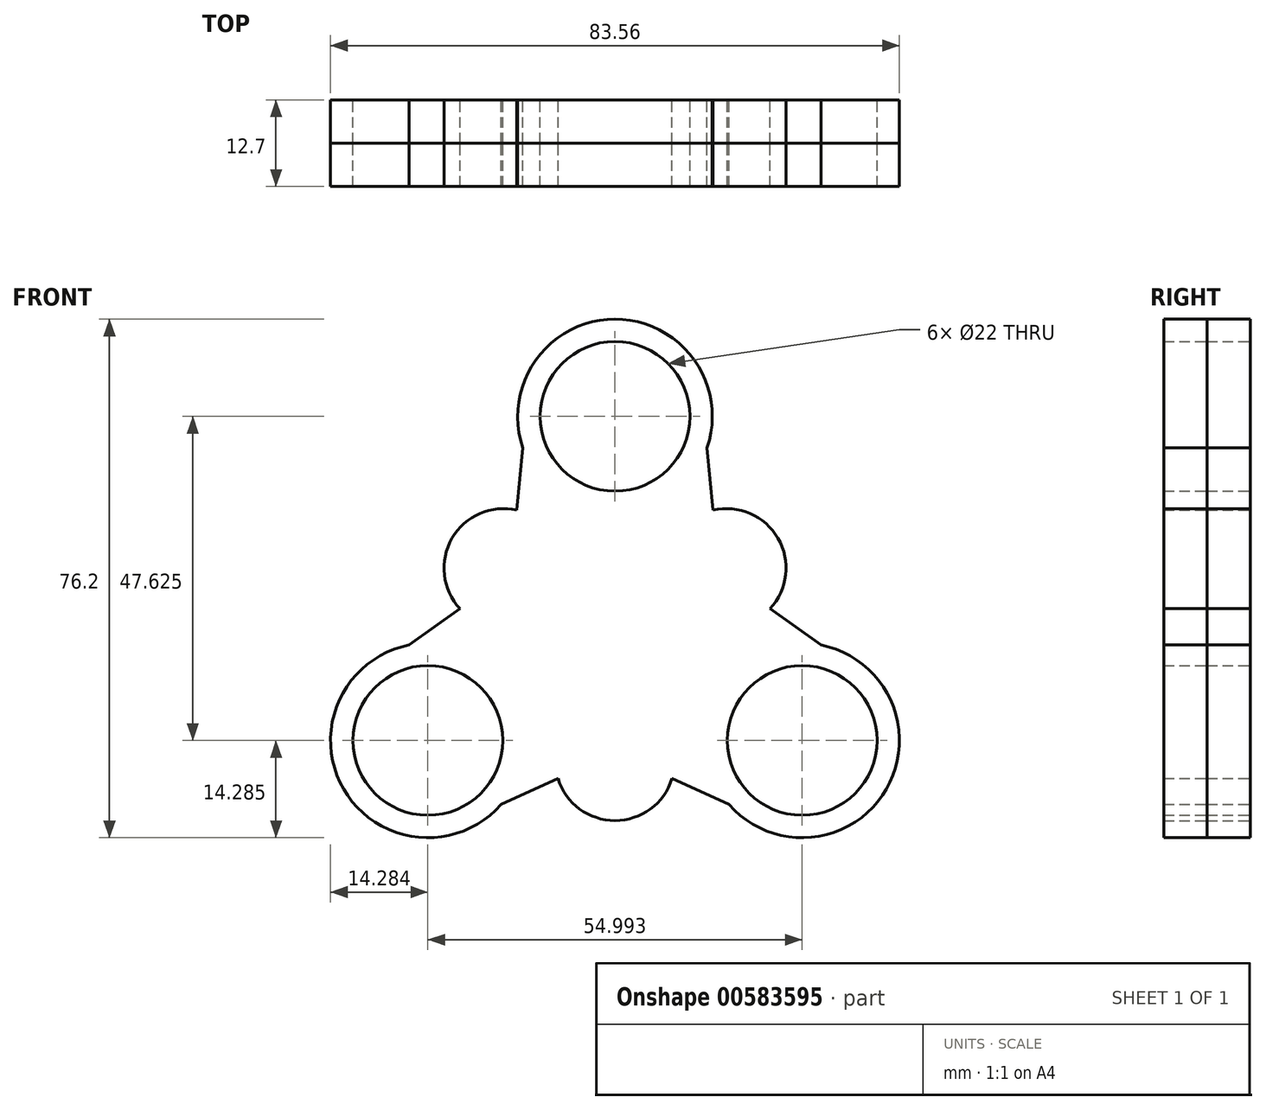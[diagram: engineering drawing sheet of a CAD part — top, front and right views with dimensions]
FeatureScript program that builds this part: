
annotation { "Feature Type Name" : "Feature", "Feature Type Description" : "" }
export const myFeature = defineFeature(function(context is Context, id is Id, definition is map)
    precondition{}
    {
        {
            var Q0;
            Q0=qCreatedBy(makeId("Front.planeOp"),FACE);
            var sketch = newSketch(context, id + "F0", { "sketchPlane" : qUnion([Q0])});
            skCircle(sketch, "E0", {"center": v(0, 0) * mm, "radius": 14.29 * mm});
            skCircle(sketch, "E1", {"center": v(0, 0) * mm, "radius": 11 * mm});
            skCircle(sketch, "E2", {"center": v(0, 31.75) * mm, "radius": 14.29 * mm});
            skCircle(sketch, "E3", {"center": v(0, 31.75) * mm, "radius": 11 * mm});
            skCircle(sketch, "E4.1.0", {"center": v(-27.5, -15.87) * mm, "radius": 14.29 * mm});
            skCircle(sketch, "E4.1.1", {"center": v(-27.5, -15.87) * mm, "radius": 11 * mm});
            skCircle(sketch, "E4.2.0", {"center": v(27.5, -15.88) * mm, "radius": 14.29 * mm});
            skCircle(sketch, "E4.2.1", {"center": v(27.5, -15.88) * mm, "radius": 11 * mm});
            skSolve(sketch);
        }
        {
            var Q0;
            Q0=qCreatedBy(makeId("Front.planeOp"),FACE);
            var sketch = newSketch(context, id + "F1", { "sketchPlane" : qUnion([Q0])});
            skCircle(sketch, "E5.0", {"center": v(0, 31.75) * mm, "radius": 14.29 * mm});
            skCircle(sketch, "E6.0", {"center": v(-27.5, -15.87) * mm, "radius": 14.29 * mm});
            skCircle(sketch, "E7.0", {"center": v(0, 0) * mm, "radius": 14.29 * mm});
            skCircle(sketch, "E8.0", {"center": v(27.5, -15.88) * mm, "radius": 14.29 * mm});
            skArc(sketch, "E9", {"start": v(-30.26, -1.86) * mm, "mid": v(-15.3, 8.84) * mm, "end": v(-13.52, 27.13) * mm});
            skArc(sketch, "E10", {"start": v(13.52, 27.13) * mm, "mid": v(15.3, 8.84) * mm, "end": v(30.26, -1.86) * mm});
            skArc(sketch, "E11", {"start": v(16.74, -25.28) * mm, "mid": v(0, -17.67) * mm, "end": v(-16.74, -25.28) * mm});
            skText(sketch, "E12", { "text": "KITSA", "fontName": "OpenSans-Regular.ttf"});
            skText(sketch, "E13", { "text": "TENNIS", "fontName": "OpenSans-Regular.ttf"});
            const initialGuessF1  = {"E12": [-0.0048, 0.01442, 1, 0, 0.00286], "E13": [-0.00896, -0.0182, 1, 0, 0.00381]};
            skSetInitialGuess(sketch, initialGuessF1);
            skSolve(sketch);
        }
        {
            var Q0;
            Q0=makeQuery(id+"F0.imprint","IMPRINT",FACE,{"disambiguationData":[TD([[makeQuery(id+"F0.imprint","IMPRINT",EDGE,{"derivedFrom":sQuery(id+"F0.wireOp",EDGE,"E2")}),1.0]])]});
            var Q1;
            Q1=makeQuery(id+"F1.imprint","IMPRINT",FACE,{"disambiguationData":[TD([[makeQuery(id+"F1.imprint","IMPRINT",EDGE,{"derivedFrom":sQuery(id+"F1.wireOp",EDGE,"E7.0")}),-1.0]])]});
            var Q2;
            Q2=makeQuery(id+"F0.imprint","IMPRINT",FACE,{"disambiguationData":[TD([[makeQuery(id+"F0.imprint","IMPRINT",EDGE,{"derivedFrom":sQuery(id+"F0.wireOp",EDGE,"E0")}),1.0]])]});
            var Q3;
            Q3=makeQuery(id+"F0.imprint","IMPRINT",FACE,{"disambiguationData":[TD([[makeQuery(id+"F0.imprint","IMPRINT",EDGE,{"derivedFrom":sQuery(id+"F0.wireOp",EDGE,"E4.1.0")}),1.0]])]});
            var Q4;
            Q4=makeQuery(id+"F0.imprint","IMPRINT",FACE,{"disambiguationData":[TD([[makeQuery(id+"F0.imprint","IMPRINT",EDGE,{"derivedFrom":sQuery(id+"F0.wireOp",EDGE,"E4.2.0")}),1.0]])]});
            extrude(context, id + "F2", {"entities" : qUnion([Q0, Q1, Q2, Q3, Q4]), "depth" : 6.35 * mm, "offsetDistance" : 25.4 * mm});
        }
        {
            var Q0;
            Q0=qCreatedBy(makeId("Front.planeOp"),FACE);
            var sketch = newSketch(context, id + "F3", { "sketchPlane" : qUnion([Q0])});
            skCircle(sketch, "E14.0", {"center": v(0, 31.75) * mm, "radius": 14.29 * mm});
            skArc(sketch, "E15.0", {"start": v(-30.26, -1.86) * mm, "mid": v(-15.3, 8.84) * mm, "end": v(-13.52, 27.13) * mm});
            skCircle(sketch, "E16.0", {"center": v(-27.5, -15.87) * mm, "radius": 14.29 * mm});
            skCircle(sketch, "E17.0", {"center": v(27.5, -15.88) * mm, "radius": 14.29 * mm});
            skArc(sketch, "E18.0", {"start": v(13.52, 27.13) * mm, "mid": v(15.3, 8.84) * mm, "end": v(30.26, -1.86) * mm});
            skArc(sketch, "E19.0", {"start": v(16.74, -25.28) * mm, "mid": v(11.15, -20.67) * mm, "end": v(4.37, -18.1) * mm});
            skCircle(sketch, "E20.0", {"center": v(0, 0) * mm, "radius": 14.29 * mm});
            skArc(sketch, "E20.1", {"start": v(16.74, -25.28) * mm, "mid": v(0, -17.67) * mm, "end": v(-16.74, -25.28) * mm});
            skLineSegment(sketch, "E20.2", {"start": v(-8.96, -14.4) * mm, "end": v(9.36, -14.4) * mm});
            skLineSegment(sketch, "E20.3", {"start": v(-8.96, -18.2) * mm, "end": v(-8.96, -14.4) * mm});
            skLineSegment(sketch, "E20.4", {"start": v(9.36, -18.2) * mm, "end": v(9.36, -14.4) * mm});
            skLineSegment(sketch, "E20.6", {"start": v(-8.96, -18.2) * mm, "end": v(9.36, -18.2) * mm});
            skCircle(sketch, "E20.7", {"center": v(0, 31.75) * mm, "radius": 11 * mm});
            skCircle(sketch, "E20.8", {"center": v(0, 0) * mm, "radius": 11 * mm});
            skCircle(sketch, "E20.9", {"center": v(27.5, -15.88) * mm, "radius": 11 * mm});
            skCircle(sketch, "E21.0", {"center": v(-27.5, -15.87) * mm, "radius": 11 * mm});
            skSolve(sketch);
        }
        {
            var Q0;
            Q0=qCreatedBy(makeId("Front.planeOp"),FACE);
            var sketch = newSketch(context, id + "F4", { "sketchPlane" : qUnion([Q0])});
            skCircle(sketch, "E22.0", {"center": v(0, 31.75) * mm, "radius": 14.29 * mm});
            skArc(sketch, "E23.0", {"start": v(-30.26, -1.86) * mm, "mid": v(-15.3, 8.84) * mm, "end": v(-13.52, 27.13) * mm});
            skCircle(sketch, "E24.0", {"center": v(-27.5, -15.87) * mm, "radius": 14.29 * mm});
            skArc(sketch, "E25.0", {"start": v(16.74, -25.28) * mm, "mid": v(11.15, -20.67) * mm, "end": v(4.37, -18.1) * mm});
            skCircle(sketch, "E26.0", {"center": v(27.5, -15.88) * mm, "radius": 14.29 * mm});
            skArc(sketch, "E27.0", {"start": v(13.52, 27.13) * mm, "mid": v(15.3, 8.84) * mm, "end": v(30.26, -1.86) * mm});
            skLineSegment(sketch, "E28", {"start": v(-15.3, 8.84) * mm, "end": v(-13.52, 27.13) * mm});
            skLineSegment(sketch, "E29", {"start": v(-15.3, 8.84) * mm, "end": v(-30.26, -1.86) * mm});
            skLineSegment(sketch, "E30.1.0", {"start": v(0, -17.67) * mm, "end": v(-16.74, -25.28) * mm});
            skLineSegment(sketch, "E30.1.1", {"start": v(0, -17.67) * mm, "end": v(16.74, -25.28) * mm});
            skLineSegment(sketch, "E30.2.0", {"start": v(15.3, 8.84) * mm, "end": v(30.26, -1.86) * mm});
            skLineSegment(sketch, "E30.2.1", {"start": v(15.3, 8.84) * mm, "end": v(13.52, 27.13) * mm});
            skPoint(sketch, "E30.center", {"position": v(0, 0) * mm});
            skSolve(sketch);
        }
        {
            var Q0;
            {var subQ0=sQuery(id+"F4.wireOp",EDGE,"E28");Q0=makeQuery(id+"F4.imprint","IMPRINT",FACE,{"disambiguationData":[TD([[makeQuery(id+"F4.imprint","IMPRINT",EDGE,{"derivedFrom":subQ0}),-1.0]])]});}
            var Q1;
            {var subQ0=sQuery(id+"F4.wireOp",EDGE,"E29");Q1=makeQuery(id+"F4.imprint","IMPRINT",FACE,{"disambiguationData":[TD([[makeQuery(id+"F4.imprint","IMPRINT",EDGE,{"derivedFrom":subQ0}),1.0]])]});}
            var Q2;
            {var subQ0=sQuery(id+"F4.wireOp",EDGE,"E30.2.1");Q2=makeQuery(id+"F4.imprint","IMPRINT",FACE,{"disambiguationData":[TD([[makeQuery(id+"F4.imprint","IMPRINT",EDGE,{"derivedFrom":subQ0}),1.0]])]});}
            var Q3;
            {var subQ0=sQuery(id+"F4.wireOp",EDGE,"E30.2.0");Q3=makeQuery(id+"F4.imprint","IMPRINT",FACE,{"disambiguationData":[TD([[makeQuery(id+"F4.imprint","IMPRINT",EDGE,{"derivedFrom":subQ0}),-1.0]])]});}
            var Q4;
            {var subQ0=sQuery(id+"F4.wireOp",EDGE,"E30.1.1");Q4=makeQuery(id+"F4.imprint","IMPRINT",FACE,{"disambiguationData":[TD([[makeQuery(id+"F4.imprint","IMPRINT",EDGE,{"derivedFrom":subQ0}),1.0]])]});}
            var Q5;
            {var subQ0=sQuery(id+"F4.wireOp",EDGE,"E30.1.0");Q5=makeQuery(id+"F4.imprint","IMPRINT",FACE,{"disambiguationData":[TD([[makeQuery(id+"F4.imprint","IMPRINT",EDGE,{"derivedFrom":subQ0}),-1.0]])]});}
            extrude(context, id + "F5", {"entities" : qUnion([Q0, Q1, Q2, Q3, Q4, Q5]), "operationType" : NewBodyOperationType.ADD, "depth" : 6.35 * mm, "offsetDistance" : 25.4 * mm});
        }
        {
            var Q0;
            Q0=qCreatedBy(makeId("Front.planeOp"),FACE);
            var sketch = newSketch(context, id + "F6", { "sketchPlane" : qUnion([Q0])});
            skCircle(sketch, "E31.0", {"center": v(0, 31.75) * mm, "radius": 14.29 * mm});
            skLineSegment(sketch, "E32.0", {"start": v(-15.3, 8.84) * mm, "end": v(-13.52, 27.13) * mm});
            skLineSegment(sketch, "E33.0", {"start": v(-15.3, 8.84) * mm, "end": v(-30.26, -1.86) * mm});
            skCircle(sketch, "E34.0", {"center": v(-27.5, -15.87) * mm, "radius": 14.29 * mm});
            skLineSegment(sketch, "E35.0", {"start": v(0, -17.67) * mm, "end": v(-16.74, -25.28) * mm});
            skLineSegment(sketch, "E36.0", {"start": v(0, -17.67) * mm, "end": v(16.74, -25.28) * mm});
            skLineSegment(sketch, "E37.0", {"start": v(15.3, 8.84) * mm, "end": v(30.26, -1.86) * mm});
            skLineSegment(sketch, "E38.0", {"start": v(15.3, 8.84) * mm, "end": v(13.52, 27.13) * mm});
            skCircle(sketch, "E39.0", {"center": v(27.5, -15.88) * mm, "radius": 14.29 * mm});
            skArc(sketch, "E40", {"start": v(-14.41, 17.98) * mm, "mid": v(-23.94, 13.82) * mm, "end": v(-22.78, 3.49) * mm});
            skArc(sketch, "E41.1.0", {"start": v(-8.37, -21.47) * mm, "mid": v(0, -27.65) * mm, "end": v(8.37, -21.47) * mm});
            skArc(sketch, "E41.2.0", {"start": v(22.78, 3.49) * mm, "mid": v(23.94, 13.82) * mm, "end": v(14.41, 17.98) * mm});
            skPoint(sketch, "E41.center", {"position": v(0, 0) * mm});
            skSolve(sketch);
        }
        {
            var Q0;
            {var subQ3=sQuery(id+"F6.wireOp",EDGE,"E40");Q0=makeQuery(id+"F6.imprint","IMPRINT",FACE,{"disambiguationData":[TD([[makeQuery(id+"F6.imprint","IMPRINT",EDGE,{"derivedFrom":subQ3}),1.0]])]});}
            var Q1;
            {var subQ3=sQuery(id+"F6.wireOp",EDGE,"E41.2.0");Q1=makeQuery(id+"F6.imprint","IMPRINT",FACE,{"disambiguationData":[TD([[makeQuery(id+"F6.imprint","IMPRINT",EDGE,{"derivedFrom":subQ3}),1.0]])]});}
            var Q2;
            {var subQ3=sQuery(id+"F6.wireOp",EDGE,"E41.1.0");Q2=makeQuery(id+"F6.imprint","IMPRINT",FACE,{"disambiguationData":[TD([[makeQuery(id+"F6.imprint","IMPRINT",EDGE,{"derivedFrom":subQ3}),1.0]])]});}
            extrude(context, id + "F7", {"entities" : qUnion([Q0, Q1, Q2]), "operationType" : NewBodyOperationType.ADD, "depth" : 6.35 * mm, "offsetDistance" : 25.4 * mm});
        }
        {
            var Q0;
            Q0=makeQuery(id+"F7.boolean.opBoolean","MERGE",FACE,{"derivedFrom":[makeQuery(id+"F5.boolean.opBoolean","MERGE",FACE,{"derivedFrom":[makeQuery(id+"F2.opExtrude","CAP_FACE",FACE,{"disambiguationData":[OSD([sQuery(id+"F1.wireOp",EDGE,"E5.0"),sQuery(id+"F1.wireOp",EDGE,"E6.0"),sQuery(id+"F1.wireOp",EDGE,"E7.0"),sQuery(id+"F1.wireOp",EDGE,"E8.0"),sQuery(id+"F1.wireOp",EDGE,"E9"),sQuery(id+"F1.wireOp",EDGE,"E10"),sQuery(id+"F1.wireOp",EDGE,"E11"),sQuery(id+"F1.wireOp",EDGE,"E12.sketch_text.stroke-0"),sQuery(id+"F1.wireOp",EDGE,"E12.sketch_text.stroke-1"),sQuery(id+"F1.wireOp",EDGE,"E12.sketch_text.stroke-2"),sQuery(id+"F1.wireOp",EDGE,"E12.sketch_text.stroke-3"),sQuery(id+"F1.wireOp",EDGE,"E12.sketch_text.stroke-4"),sQuery(id+"F1.wireOp",EDGE,"E12.sketch_text.stroke-5"),sQuery(id+"F1.wireOp",EDGE,"E12.sketch_text.stroke-6"),sQuery(id+"F1.wireOp",EDGE,"E12.sketch_text.stroke-7"),sQuery(id+"F1.wireOp",EDGE,"E12.sketch_text.stroke-8"),sQuery(id+"F1.wireOp",EDGE,"E12.sketch_text.stroke-9"),sQuery(id+"F1.wireOp",EDGE,"E12.sketch_text.stroke-10"),sQuery(id+"F1.wireOp",EDGE,"E12.sketch_text.stroke-11"),sQuery(id+"F1.wireOp",EDGE,"E12.sketch_text.stroke-12"),sQuery(id+"F1.wireOp",EDGE,"E12.sketch_text.stroke-13"),sQuery(id+"F1.wireOp",EDGE,"E12.sketch_text.stroke-14"),sQuery(id+"F1.wireOp",EDGE,"E12.sketch_text.stroke-15"),sQuery(id+"F1.wireOp",EDGE,"E12.sketch_text.stroke-16"),sQuery(id+"F1.wireOp",EDGE,"E12.sketch_text.stroke-17"),sQuery(id+"F1.wireOp",EDGE,"E12.sketch_text.stroke-18"),sQuery(id+"F1.wireOp",EDGE,"E12.sketch_text.stroke-19"),sQuery(id+"F1.wireOp",EDGE,"E12.sketch_text.stroke-20"),sQuery(id+"F1.wireOp",EDGE,"E12.sketch_text.stroke-21"),sQuery(id+"F1.wireOp",EDGE,"E12.sketch_text.stroke-22"),sQuery(id+"F1.wireOp",EDGE,"E12.sketch_text.stroke-23"),sQuery(id+"F1.wireOp",EDGE,"E12.sketch_text.stroke-24"),sQuery(id+"F1.wireOp",EDGE,"E12.sketch_text.stroke-25"),sQuery(id+"F1.wireOp",EDGE,"E12.sketch_text.stroke-26"),sQuery(id+"F1.wireOp",EDGE,"E12.sketch_text.stroke-27"),sQuery(id+"F1.wireOp",EDGE,"E12.sketch_text.stroke-28"),sQuery(id+"F1.wireOp",EDGE,"E12.sketch_text.stroke-29"),sQuery(id+"F1.wireOp",EDGE,"E12.sketch_text.stroke-30"),sQuery(id+"F1.wireOp",EDGE,"E12.sketch_text.stroke-31"),sQuery(id+"F1.wireOp",EDGE,"E12.sketch_text.stroke-32"),sQuery(id+"F1.wireOp",EDGE,"E12.sketch_text.stroke-33"),sQuery(id+"F1.wireOp",EDGE,"E12.sketch_text.stroke-34"),sQuery(id+"F1.wireOp",EDGE,"E12.sketch_text.stroke-35"),sQuery(id+"F1.wireOp",EDGE,"E12.sketch_text.stroke-36"),sQuery(id+"F1.wireOp",EDGE,"E12.sketch_text.stroke-37"),sQuery(id+"F1.wireOp",EDGE,"E12.sketch_text.stroke-38"),sQuery(id+"F1.wireOp",EDGE,"E12.sketch_text.stroke-39"),sQuery(id+"F1.wireOp",EDGE,"E12.sketch_text.stroke-40"),sQuery(id+"F1.wireOp",EDGE,"E12.sketch_text.stroke-41"),sQuery(id+"F1.wireOp",EDGE,"E12.sketch_text.stroke-42"),sQuery(id+"F1.wireOp",EDGE,"E12.sketch_text.stroke-43"),sQuery(id+"F1.wireOp",EDGE,"E12.sketch_text.stroke-44"),sQuery(id+"F1.wireOp",EDGE,"E12.sketch_text.stroke-45"),sQuery(id+"F1.wireOp",EDGE,"E12.sketch_text.stroke-46"),sQuery(id+"F1.wireOp",EDGE,"E12.sketch_text.stroke-47"),sQuery(id+"F1.wireOp",EDGE,"E12.sketch_text.stroke-48"),sQuery(id+"F1.wireOp",EDGE,"E12.sketch_text.stroke-49"),sQuery(id+"F1.wireOp",EDGE,"E12.sketch_text.stroke-50"),sQuery(id+"F1.wireOp",EDGE,"E12.sketch_text.stroke-51"),sQuery(id+"F1.wireOp",EDGE,"E12.sketch_text.stroke-52"),sQuery(id+"F1.wireOp",EDGE,"E12.sketch_text.stroke-53"),sQuery(id+"F1.wireOp",EDGE,"E12.sketch_text.stroke-54"),sQuery(id+"F1.wireOp",EDGE,"E12.sketch_text.stroke-55"),sQuery(id+"F1.wireOp",EDGE,"E12.sketch_text.stroke-56"),sQuery(id+"F1.wireOp",EDGE,"E13.sketch_text.stroke-0"),sQuery(id+"F1.wireOp",EDGE,"E13.sketch_text.stroke-1"),sQuery(id+"F1.wireOp",EDGE,"E13.sketch_text.stroke-2"),sQuery(id+"F1.wireOp",EDGE,"E13.sketch_text.stroke-3"),sQuery(id+"F1.wireOp",EDGE,"E13.sketch_text.stroke-4"),sQuery(id+"F1.wireOp",EDGE,"E13.sketch_text.stroke-5"),sQuery(id+"F1.wireOp",EDGE,"E13.sketch_text.stroke-6"),sQuery(id+"F1.wireOp",EDGE,"E13.sketch_text.stroke-7"),sQuery(id+"F1.wireOp",EDGE,"E13.sketch_text.stroke-8"),sQuery(id+"F1.wireOp",EDGE,"E13.sketch_text.stroke-9"),sQuery(id+"F1.wireOp",EDGE,"E13.sketch_text.stroke-10"),sQuery(id+"F1.wireOp",EDGE,"E13.sketch_text.stroke-11"),sQuery(id+"F1.wireOp",EDGE,"E13.sketch_text.stroke-12"),sQuery(id+"F1.wireOp",EDGE,"E13.sketch_text.stroke-13"),sQuery(id+"F1.wireOp",EDGE,"E13.sketch_text.stroke-14"),sQuery(id+"F1.wireOp",EDGE,"E13.sketch_text.stroke-15"),sQuery(id+"F1.wireOp",EDGE,"E13.sketch_text.stroke-16"),sQuery(id+"F1.wireOp",EDGE,"E13.sketch_text.stroke-17"),sQuery(id+"F1.wireOp",EDGE,"E13.sketch_text.stroke-18"),sQuery(id+"F1.wireOp",EDGE,"E13.sketch_text.stroke-19"),sQuery(id+"F1.wireOp",EDGE,"E13.sketch_text.stroke-26"),sQuery(id+"F1.wireOp",EDGE,"E13.sketch_text.stroke-27"),sQuery(id+"F1.wireOp",EDGE,"E13.sketch_text.stroke-28"),sQuery(id+"F1.wireOp",EDGE,"E13.sketch_text.stroke-29"),sQuery(id+"F1.wireOp",EDGE,"E13.sketch_text.stroke-30"),sQuery(id+"F1.wireOp",EDGE,"E13.sketch_text.stroke-31"),sQuery(id+"F1.wireOp",EDGE,"E13.sketch_text.stroke-32"),sQuery(id+"F1.wireOp",EDGE,"E13.sketch_text.stroke-33"),sQuery(id+"F1.wireOp",EDGE,"E13.sketch_text.stroke-34"),sQuery(id+"F1.wireOp",EDGE,"E13.sketch_text.stroke-41"),sQuery(id+"F1.wireOp",EDGE,"E13.sketch_text.stroke-42"),sQuery(id+"F1.wireOp",EDGE,"E13.sketch_text.stroke-43"),sQuery(id+"F1.wireOp",EDGE,"E13.sketch_text.stroke-44"),sQuery(id+"F1.wireOp",EDGE,"E13.sketch_text.stroke-45"),sQuery(id+"F1.wireOp",EDGE,"E13.sketch_text.stroke-46"),sQuery(id+"F1.wireOp",EDGE,"E13.sketch_text.stroke-47"),sQuery(id+"F1.wireOp",EDGE,"E13.sketch_text.stroke-48"),sQuery(id+"F1.wireOp",EDGE,"E13.sketch_text.stroke-49"),sQuery(id+"F1.wireOp",EDGE,"E13.sketch_text.stroke-50"),sQuery(id+"F1.wireOp",EDGE,"E13.sketch_text.stroke-51"),sQuery(id+"F1.wireOp",EDGE,"E13.sketch_text.stroke-52"),sQuery(id+"F1.wireOp",EDGE,"E13.sketch_text.stroke-53"),sQuery(id+"F1.wireOp",EDGE,"E13.sketch_text.stroke-54"),sQuery(id+"F1.wireOp",EDGE,"E13.sketch_text.stroke-55"),sQuery(id+"F1.wireOp",EDGE,"E13.sketch_text.stroke-56"),sQuery(id+"F1.wireOp",EDGE,"E13.sketch_text.stroke-57"),sQuery(id+"F1.wireOp",EDGE,"E13.sketch_text.stroke-58"),sQuery(id+"F1.wireOp",EDGE,"E13.sketch_text.stroke-59"),sQuery(id+"F1.wireOp",EDGE,"E13.sketch_text.stroke-60"),sQuery(id+"F1.wireOp",EDGE,"E13.sketch_text.stroke-61"),sQuery(id+"F1.wireOp",EDGE,"E13.sketch_text.stroke-62"),sQuery(id+"F1.wireOp",EDGE,"E13.sketch_text.stroke-63"),sQuery(id+"F1.wireOp",EDGE,"E13.sketch_text.stroke-64"),sQuery(id+"F1.wireOp",EDGE,"E13.sketch_text.stroke-65"),sQuery(id+"F1.wireOp",EDGE,"E13.sketch_text.stroke-66"),sQuery(id+"F1.wireOp",EDGE,"E13.sketch_text.stroke-67"),sQuery(id+"F1.wireOp",EDGE,"E13.sketch_text.stroke-68"),sQuery(id+"F1.wireOp",EDGE,"E13.sketch_text.stroke-69"),sQuery(id+"F1.wireOp",EDGE,"E13.sketch_text.stroke-70"),sQuery(id+"F1.wireOp",EDGE,"E13.sketch_text.stroke-71"),sQuery(id+"F1.wireOp",EDGE,"E13.sketch_text.stroke-72"),sQuery(id+"F1.wireOp",EDGE,"E13.sketch_text.stroke-73"),sQuery(id+"F1.wireOp",EDGE,"E13.sketch_text.stroke-74"),sQuery(id+"F1.wireOp",EDGE,"E13.sketch_text.stroke-75"),sQuery(id+"F1.wireOp",EDGE,"E13.sketch_text.stroke-76"),sQuery(id+"F1.wireOp",EDGE,"E13.sketch_text.stroke-77"),sQuery(id+"F1.wireOp",EDGE,"E13.sketch_text.stroke-78")])],"isStart":false}),makeQuery(id+"F5.opExtrude","CAP_FACE",FACE,{"disambiguationData":[OSD([sQuery(id+"F4.wireOp",EDGE,"E24.0"),sQuery(id+"F4.wireOp",EDGE,"E26.0"),sQuery(id+"F4.wireOp",EDGE,"E22.0"),sQuery(id+"F4.wireOp",EDGE,"E28"),sQuery(id+"F4.wireOp",EDGE,"E29"),sQuery(id+"F4.wireOp",EDGE,"E30.1.0"),sQuery(id+"F4.wireOp",EDGE,"E30.1.1"),sQuery(id+"F4.wireOp",EDGE,"E30.2.0"),sQuery(id+"F4.wireOp",EDGE,"E30.2.1")])],"isStart":false})]}),makeQuery(id+"F7.opExtrude","CAP_FACE",FACE,{"disambiguationData":[OSD([sQuery(id+"F6.wireOp",EDGE,"E32.0"),sQuery(id+"F6.wireOp",EDGE,"E33.0"),sQuery(id+"F6.wireOp",EDGE,"E40")])],"isStart":false}),makeQuery(id+"F7.opExtrude","CAP_FACE",FACE,{"disambiguationData":[OSD([sQuery(id+"F6.wireOp",EDGE,"E35.0"),sQuery(id+"F6.wireOp",EDGE,"E36.0"),sQuery(id+"F6.wireOp",EDGE,"E41.1.0")])],"isStart":false}),makeQuery(id+"F7.opExtrude","CAP_FACE",FACE,{"disambiguationData":[OSD([sQuery(id+"F6.wireOp",EDGE,"E37.0"),sQuery(id+"F6.wireOp",EDGE,"E38.0"),sQuery(id+"F6.wireOp",EDGE,"E41.2.0")])],"isStart":false})]});
            extrude(context, id + "F8", {"entities" : qUnion([Q0]), "depth" : 6.35 * mm, "offsetDistance" : 25.4 * mm});
        }
    });
